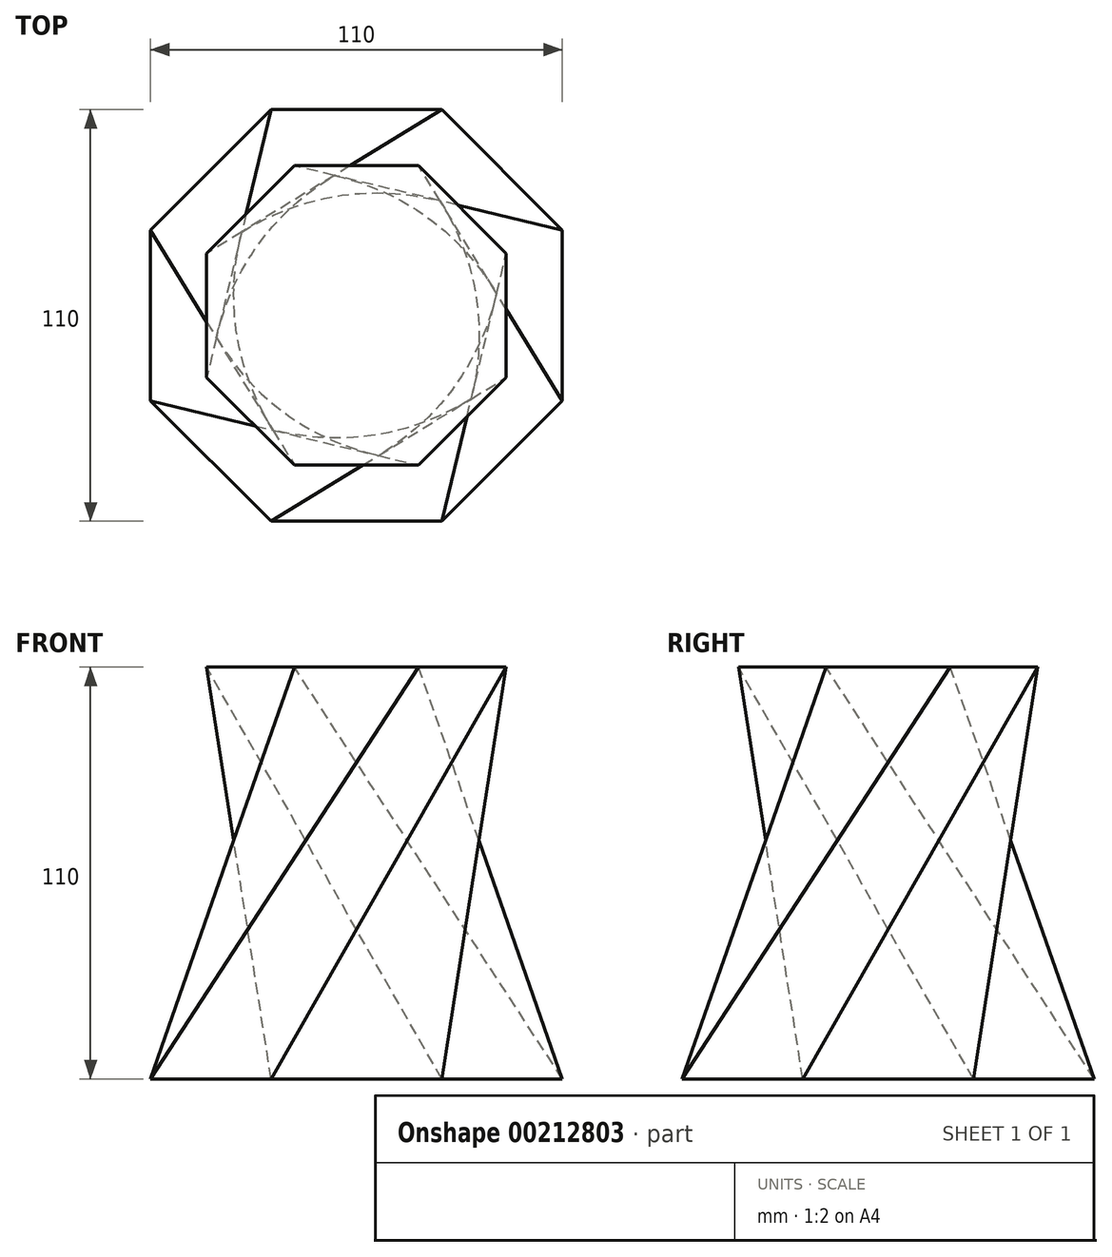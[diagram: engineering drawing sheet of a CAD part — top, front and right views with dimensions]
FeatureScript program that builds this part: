
annotation { "Feature Type Name" : "Feature", "Feature Type Description" : "" }
export const myFeature = defineFeature(function(context is Context, id is Id, definition is map)
    precondition{}
    {
        {
            var Q0;
            Q0=qCreatedBy(makeId("Top.planeOp"),FACE);
            cPlane(context, id + "F0", {"entities" : qUnion([Q0]), "cplaneType" : CPlaneType.OFFSET, "offset" : 110 * mm, "width" : 150 * mm, "height" : 150 * mm});
        }
        {
            var Q0;
            Q0=qCreatedBy(makeId("Top.planeOp"),FACE);
            cPlane(context, id + "F1", {"entities" : qUnion([Q0]), "cplaneType" : CPlaneType.OFFSET, "offset" : 5 * mm, "width" : 150 * mm, "height" : 150 * mm});
        }
        {
            var Q0;
            Q0=qCreatedBy(makeId("Top.planeOp"),FACE);
            var sketch = newSketch(context, id + "F2", { "sketchPlane" : qUnion([Q0])});
            skCircle(sketch, "E0.cCircle", {"center": v(0, 0) * mm, "radius": 55 * mm, "construction": true});
            skLineSegment(sketch, "E0.0", {"start": v(55, 22.78) * mm, "end": v(55, -22.78) * mm});
            skLineSegment(sketch, "E0.1", {"start": v(55, -22.78) * mm, "end": v(22.78, -55) * mm});
            skLineSegment(sketch, "E0.2", {"start": v(22.78, -55) * mm, "end": v(-22.78, -55) * mm});
            skLineSegment(sketch, "E0.3", {"start": v(-22.78, -55) * mm, "end": v(-55, -22.78) * mm});
            skLineSegment(sketch, "E0.4", {"start": v(-55, -22.78) * mm, "end": v(-55, 22.78) * mm});
            skLineSegment(sketch, "E0.5", {"start": v(-55, 22.78) * mm, "end": v(-22.78, 55) * mm});
            skLineSegment(sketch, "E0.6", {"start": v(-22.78, 55) * mm, "end": v(22.78, 55) * mm});
            skLineSegment(sketch, "E0.7", {"start": v(22.78, 55) * mm, "end": v(55, 22.78) * mm});
            skPoint(sketch, "E0.0.midPoint", {"position": v(55, 0) * mm});
            skPoint(sketch, "E1.0.midPoint", {"position": v(44, 0) * mm});
            skSolve(sketch);
        }
        {
            var Q0;
            Q0=qCreatedBy(id+"F1.planeOp",FACE);
            var sketch = newSketch(context, id + "F3", { "sketchPlane" : qUnion([Q0])});
            skCircle(sketch, "E2.cCircle", {"center": v(0, 0) * mm, "radius": 27.5 * mm, "construction": true});
            skLineSegment(sketch, "E2.0", {"start": v(27.5, 11.4) * mm, "end": v(27.5, -11.4) * mm});
            skLineSegment(sketch, "E2.1", {"start": v(27.5, -11.4) * mm, "end": v(11.4, -27.5) * mm});
            skLineSegment(sketch, "E2.2", {"start": v(11.4, -27.5) * mm, "end": v(-11.4, -27.5) * mm});
            skLineSegment(sketch, "E2.3", {"start": v(-11.4, -27.5) * mm, "end": v(-27.5, -11.4) * mm});
            skLineSegment(sketch, "E2.4", {"start": v(-27.5, -11.4) * mm, "end": v(-27.5, 11.4) * mm});
            skLineSegment(sketch, "E2.5", {"start": v(-27.5, 11.4) * mm, "end": v(-11.4, 27.5) * mm});
            skLineSegment(sketch, "E2.6", {"start": v(-11.4, 27.5) * mm, "end": v(11.4, 27.5) * mm});
            skLineSegment(sketch, "E2.7", {"start": v(11.4, 27.5) * mm, "end": v(27.5, 11.4) * mm});
            skPoint(sketch, "E2.0.midPoint", {"position": v(27.5, 0) * mm});
            skSolve(sketch);
        }
        {
            var Q0;
            Q0=qCreatedBy(makeId("Top.planeOp"),FACE);
            cPlane(context, id + "F4", {"entities" : qUnion([Q0]), "cplaneType" : CPlaneType.OFFSET, "offset" : 105 * mm, "width" : 150 * mm, "height" : 150 * mm});
        }
        {
            var Q0;
            Q0=qCreatedBy(id+"F0.planeOp",FACE);
            var sketch = newSketch(context, id + "F5", { "sketchPlane" : qUnion([Q0])});
            skPoint(sketch, "E3", {"position": v(-10, 10) * mm});
            skPoint(sketch, "E4", {"position": v(10, 10) * mm});
            skSolve(sketch);
        }
        {
            var Q0;
            Q0=qCreatedBy(id+"F4.planeOp",FACE);
            var sketch = newSketch(context, id + "F6", { "sketchPlane" : qUnion([Q0])});
            skPoint(sketch, "E5", {"position": v(0, -10) * mm});
            skSolve(sketch);
        }
        {
            var Q0;
            Q0=qCreatedBy(id+"F0.planeOp",FACE);
            var sketch = newSketch(context, id + "F7", { "sketchPlane" : qUnion([Q0])});
            skCircle(sketch, "E6.cCircle", {"center": v(0, 0) * mm, "radius": 40 * mm, "construction": true});
            skLineSegment(sketch, "E6.0", {"start": v(40, 16.57) * mm, "end": v(40, -16.57) * mm});
            skLineSegment(sketch, "E6.1", {"start": v(40, -16.57) * mm, "end": v(16.57, -40) * mm});
            skLineSegment(sketch, "E6.2", {"start": v(16.57, -40) * mm, "end": v(-16.57, -40) * mm});
            skLineSegment(sketch, "E6.3", {"start": v(-16.57, -40) * mm, "end": v(-40, -16.57) * mm});
            skLineSegment(sketch, "E6.4", {"start": v(-40, -16.57) * mm, "end": v(-40, 16.57) * mm});
            skLineSegment(sketch, "E6.5", {"start": v(-40, 16.57) * mm, "end": v(-16.57, 40) * mm});
            skLineSegment(sketch, "E6.6", {"start": v(-16.57, 40) * mm, "end": v(16.57, 40) * mm});
            skLineSegment(sketch, "E6.7", {"start": v(16.57, 40) * mm, "end": v(40, 16.57) * mm});
            skPoint(sketch, "E6.0.midPoint", {"position": v(40, 0) * mm});
            skSolve(sketch);
        }
        {
            var Q0;
            Q0=qCreatedBy(id+"F0.planeOp",FACE);
            var sketch = newSketch(context, id + "F8", { "sketchPlane" : qUnion([Q0])});
            skPoint(sketch, "E7", {"position": v(0, 0) * mm});
            skCircle(sketch, "E8.cCircle", {"center": v(0, 0) * mm, "radius": 35 * mm, "construction": true});
            skLineSegment(sketch, "E8.0", {"start": v(35, 14.5) * mm, "end": v(35, -14.5) * mm});
            skLineSegment(sketch, "E8.1", {"start": v(35, -14.5) * mm, "end": v(14.5, -35) * mm});
            skLineSegment(sketch, "E8.2", {"start": v(14.5, -35) * mm, "end": v(-14.5, -35) * mm});
            skLineSegment(sketch, "E8.3", {"start": v(-14.5, -35) * mm, "end": v(-35, -14.5) * mm});
            skLineSegment(sketch, "E8.4", {"start": v(-35, -14.5) * mm, "end": v(-35, 14.5) * mm});
            skLineSegment(sketch, "E8.5", {"start": v(-35, 14.5) * mm, "end": v(-14.5, 35) * mm});
            skLineSegment(sketch, "E8.6", {"start": v(-14.5, 35) * mm, "end": v(14.5, 35) * mm});
            skLineSegment(sketch, "E8.7", {"start": v(14.5, 35) * mm, "end": v(35, 14.5) * mm});
            skPoint(sketch, "E8.0.midPoint", {"position": v(35, 0) * mm});
            skSolve(sketch);
        }
        {
            var Q0;
            Q0=makeQuery(id+"F2.imprint","IMPRINT",FACE,{"disambiguationData":[TD([[makeQuery(id+"F2.imprint","IMPRINT",EDGE,{"derivedFrom":sQuery(id+"F2.wireOp",EDGE,"E0.0")}),-1.0]])]});
            var Q1;
            Q1=makeQuery(id+"F7.imprint","IMPRINT",FACE,{"disambiguationData":[TD([[makeQuery(id+"F7.imprint","IMPRINT",EDGE,{"derivedFrom":sQuery(id+"F7.wireOp",EDGE,"E6.0")}),-1.0]])]});
            var Q2;
            Q2=sQuery(id+"F2.wireOp",VERTEX,"E0.4.start");
            var Q3;
            Q3=sQuery(id+"F7.wireOp",VERTEX,"E6.2.start");
            loft(context, id + "F9", {"sheetProfilesArray" : [{ "sheetProfileEntities" : qUnion([Q0]) }, { "sheetProfileEntities" : qUnion([Q1]) }], "matchConnections" : true, "connections" : [{ "connectionEntities" : qUnion([Q2, Q3]), "connectionEdgeQueries" : qUnion([]), "connectionEdgeParameters" : [] }]});
        }
    });
